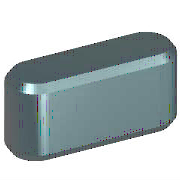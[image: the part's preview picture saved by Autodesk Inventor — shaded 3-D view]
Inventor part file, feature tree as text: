
AUTODESK INVENTOR PART (.ipt)
format: ipt  version: 2025 (Build 290162000, 162)  size: 139,776 bytes
history: native  units: mm (DEFAULTED — no unit token found)
features: plane x3, extrude x1
ambient origin geometry x8: Origin, YZ Plane, XZ Plane, XY Plane, X Axis, Y Axis, Z Axis, Center Point
bodies: Solid1 (feature_tree)
feature tree (4):
  plane  "Work Plane1"
  plane  "Work Plane2"
  extrude  "轴承体1"  Depth=9.0mm
  plane  "Work Plane3"
